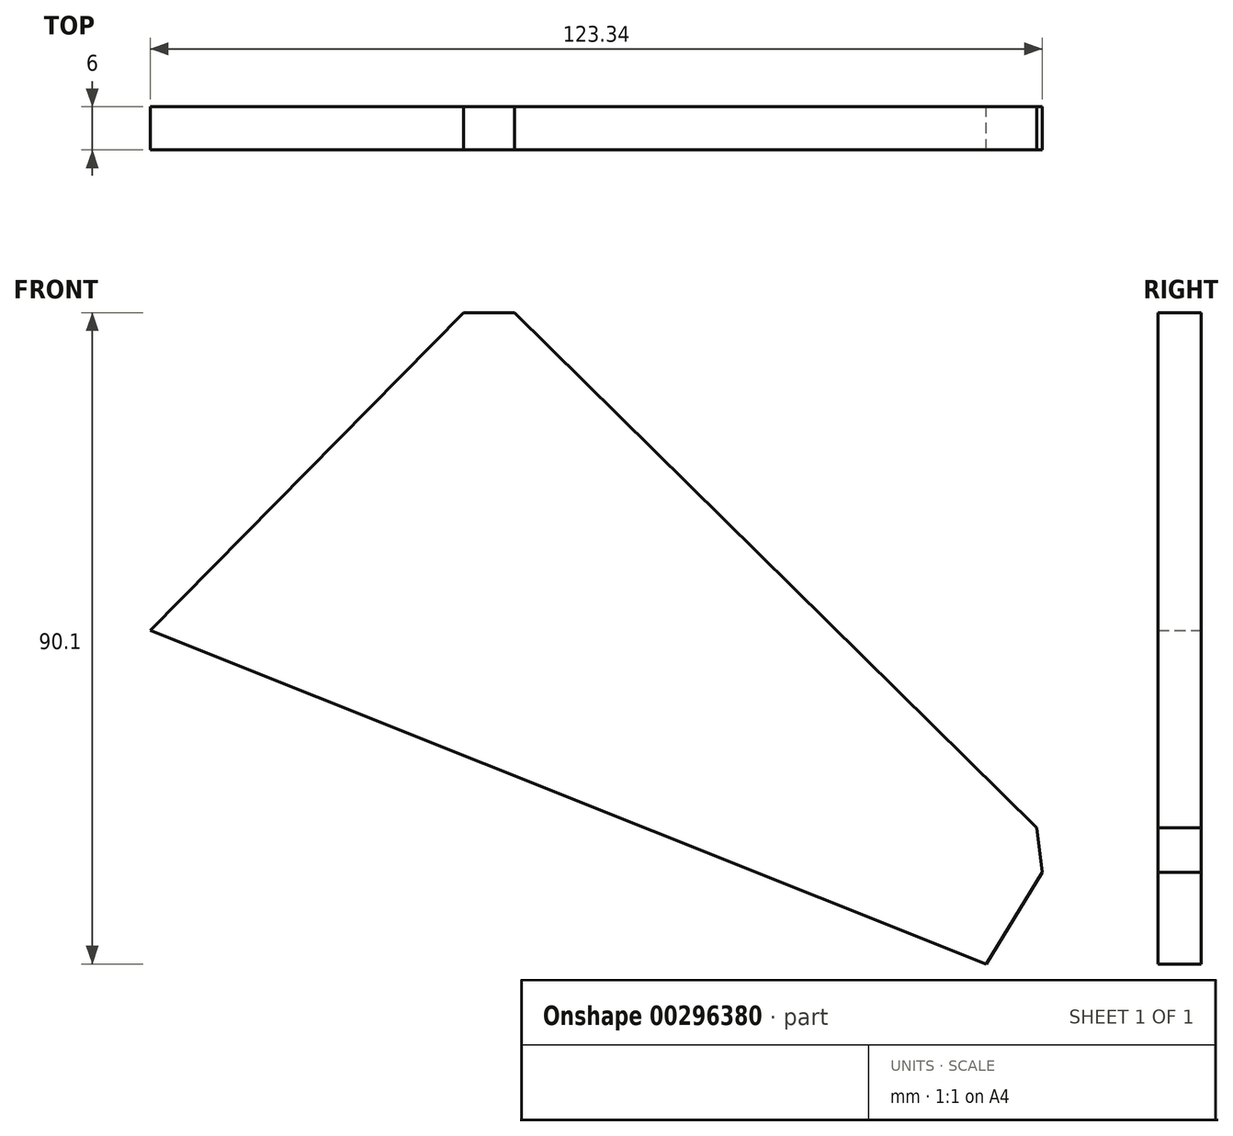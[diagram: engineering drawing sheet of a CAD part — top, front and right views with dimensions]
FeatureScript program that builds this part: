
annotation { "Feature Type Name" : "Feature", "Feature Type Description" : "" }
export const myFeature = defineFeature(function(context is Context, id is Id, definition is map)
    precondition{}
    {
        {
            var Q0;
            Q0=qCreatedBy(makeId("Front.planeOp"),FACE);
            var sketch = newSketch(context, id + "F0", { "sketchPlane" : qUnion([Q0])});
            skLineSegment(sketch, "E0", {"start": v(-319.1, 24.92) * mm, "end": v(-319.1, 76.88) * mm});
            skLineSegment(sketch, "E1", {"start": v(280.9, -98.79) * mm, "end": v(280.9, -137.14) * mm});
            skLineSegment(sketch, "E2", {"start": v(155.65, -47.45) * mm, "end": v(202.5, 0) * mm});
            skLineSegment(sketch, "E3", {"start": v(202.5, 0) * mm, "end": v(281.06, -77.57) * mm});
            skLineSegment(sketch, "E4", {"start": v(281.06, -77.57) * mm, "end": v(271.24, -93.6) * mm});
            skLineSegment(sketch, "E5", {"start": v(271.24, -93.6) * mm, "end": v(155.65, -47.45) * mm});
            skSolve(sketch);
        }
        {
            var Q0;
            Q0=makeQuery(id+"F0.imprint","IMPRINT",FACE,{"disambiguationData":[TD([[makeQuery(id+"F0.imprint","IMPRINT",EDGE,{"derivedFrom":sQuery(id+"F0.wireOp",EDGE,"E2")}),-1.0]])]});
            extrude(context, id + "F1", {"entities" : qUnion([Q0]), "depth" : 6 * mm});
        }
        {
            var Q0;
            Q0=makeQuery(id+"F1.opExtrude","SWEPT_EDGE",EDGE,{"disambiguationData":[OSD([sQuery(id+"F0.wireOp",EDGE,"E2"),sQuery(id+"F0.wireOp",EDGE,"E3")])]});
            var Q1;
            Q1=makeQuery(id+"F1.opExtrude","SWEPT_EDGE",EDGE,{"disambiguationData":[OSD([sQuery(id+"F0.wireOp",EDGE,"E3"),sQuery(id+"F0.wireOp",EDGE,"E4")])]});
            chamfer(context, id + "F2", {"entities" : qUnion([Q0, Q1]), "width" : 5 * mm, "tangentPropagation" : true});
        }
    });
